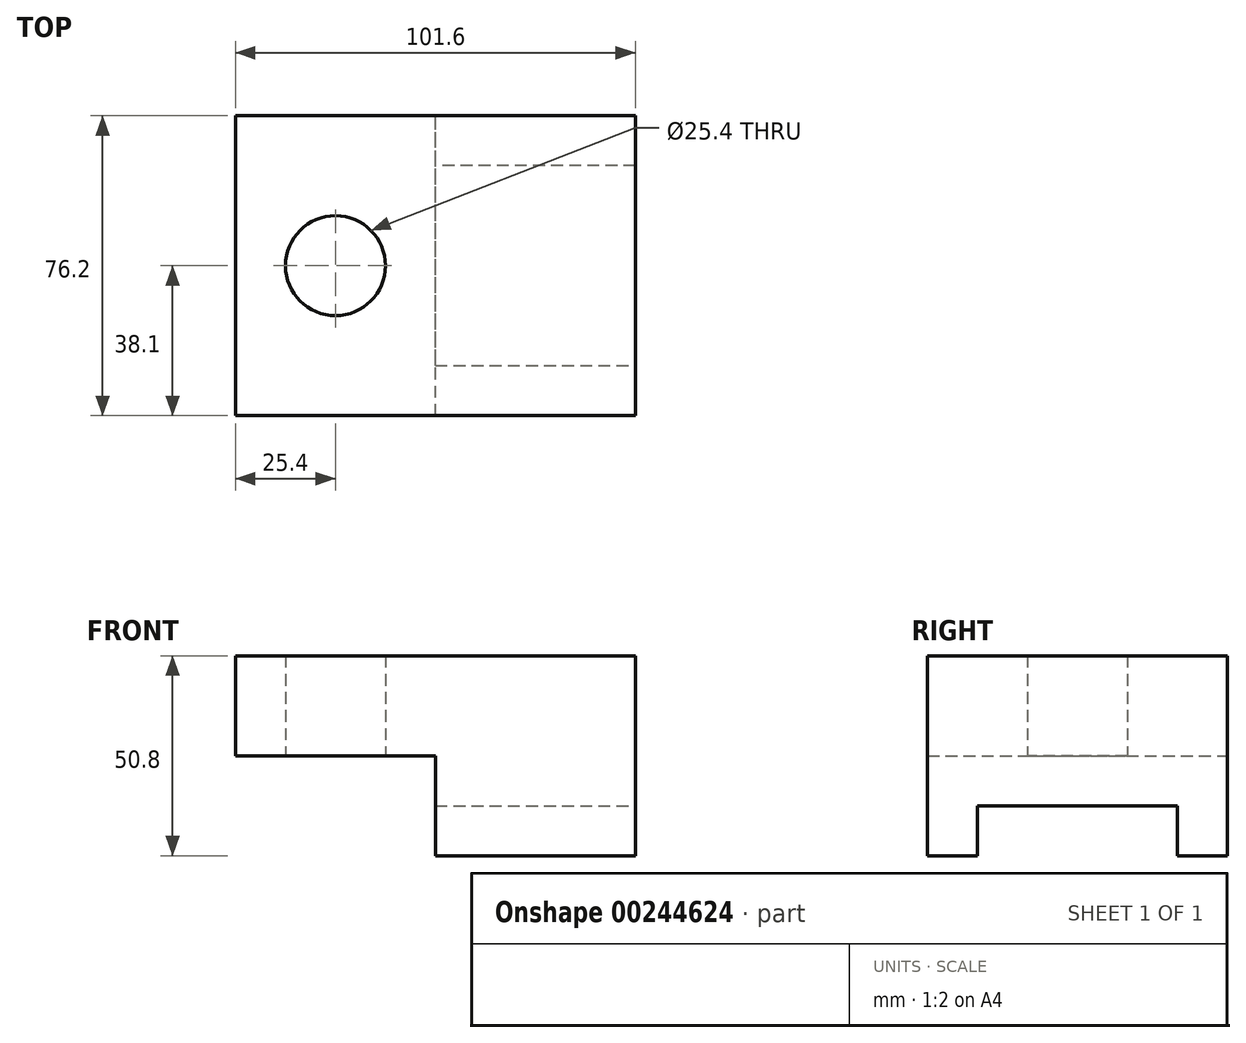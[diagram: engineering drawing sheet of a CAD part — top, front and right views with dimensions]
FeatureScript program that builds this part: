
annotation { "Feature Type Name" : "Feature", "Feature Type Description" : "" }
export const myFeature = defineFeature(function(context is Context, id is Id, definition is map)
    precondition{}
    {
        {
            var Q0;
            Q0=qCreatedBy(makeId("Top.planeOp"),FACE);
            var sketch = newSketch(context, id + "F0", { "sketchPlane" : qUnion([Q0])});
            skLineSegment(sketch, "E0.bottom", {"start": v(0, 0) * mm, "end": v(25.4, 0) * mm});
            skLineSegment(sketch, "E0.top", {"start": v(0, 25.4) * mm, "end": v(25.4, 25.4) * mm});
            skLineSegment(sketch, "E0.left", {"start": v(0, 0) * mm, "end": v(0, 25.4) * mm});
            skLineSegment(sketch, "E0.right", {"start": v(25.4, 0) * mm, "end": v(25.4, 25.4) * mm});
            skLineSegment(sketch, "E1.0.2.0", {"start": v(0, 50.8) * mm, "end": v(25.4, 50.8) * mm});
            skLineSegment(sketch, "E1.0.3.0", {"start": v(0, 76.2) * mm, "end": v(25.4, 76.2) * mm});
            skLineSegment(sketch, "E1.1.0.0", {"start": v(25.4, 0) * mm, "end": v(50.8, 0) * mm});
            skLineSegment(sketch, "E1.1.1.0", {"start": v(25.4, 25.4) * mm, "end": v(50.8, 25.4) * mm});
            skLineSegment(sketch, "E1.1.2.0", {"start": v(25.4, 50.8) * mm, "end": v(50.8, 50.8) * mm});
            skLineSegment(sketch, "E1.1.3.0", {"start": v(25.4, 76.2) * mm, "end": v(50.8, 76.2) * mm});
            skLineSegment(sketch, "E1.2.0.0", {"start": v(50.8, 0) * mm, "end": v(76.2, 0) * mm});
            skLineSegment(sketch, "E1.2.1.0", {"start": v(50.8, 25.4) * mm, "end": v(76.2, 25.4) * mm});
            skLineSegment(sketch, "E1.2.2.0", {"start": v(50.8, 50.8) * mm, "end": v(76.2, 50.8) * mm});
            skLineSegment(sketch, "E1.2.3.0", {"start": v(50.8, 76.2) * mm, "end": v(76.2, 76.2) * mm});
            skLineSegment(sketch, "E1.direction2", {"start": v(0, 0) * mm, "end": v(0, 25.4) * mm, "construction": true});
            skLineSegment(sketch, "E2", {"start": v(0, 76.2) * mm, "end": v(0, 50.8) * mm});
            skLineSegment(sketch, "E3", {"start": v(0, 50.8) * mm, "end": v(0, 25.4) * mm});
            skLineSegment(sketch, "E4", {"start": v(25.4, 76.2) * mm, "end": v(25.4, 50.8) * mm});
            skLineSegment(sketch, "E5", {"start": v(25.4, 50.8) * mm, "end": v(25.4, 25.4) * mm});
            skLineSegment(sketch, "E6", {"start": v(50.8, 76.2) * mm, "end": v(50.8, 50.8) * mm});
            skLineSegment(sketch, "E7", {"start": v(50.8, 50.8) * mm, "end": v(50.8, 25.4) * mm});
            skLineSegment(sketch, "E8", {"start": v(50.8, 25.4) * mm, "end": v(50.8, 0) * mm});
            skLineSegment(sketch, "E9", {"start": v(76.2, 76.2) * mm, "end": v(76.2, 50.8) * mm});
            skLineSegment(sketch, "E10", {"start": v(76.2, 25.4) * mm, "end": v(76.2, 0) * mm});
            skLineSegment(sketch, "E11.MirrorCS", {"start": v(0, 76.2) * mm, "end": v(-25.4, 76.2) * mm});
            skLineSegment(sketch, "E12.MirrorCS", {"start": v(-25.4, 50.8) * mm, "end": v(-25.4, 25.4) * mm});
            skLineSegment(sketch, "E13.MirrorCS", {"start": v(0, 25.4) * mm, "end": v(-25.4, 25.4) * mm});
            skLineSegment(sketch, "E14.MirrorCS", {"start": v(-25.4, 0) * mm, "end": v(-25.4, 25.4) * mm});
            skLineSegment(sketch, "E15.MirrorCS", {"start": v(0, 0) * mm, "end": v(-25.4, 0) * mm});
            skLineSegment(sketch, "E16.MirrorCS", {"start": v(0, 50.8) * mm, "end": v(-25.4, 50.8) * mm});
            skLineSegment(sketch, "E17.MirrorCS", {"start": v(-25.4, 76.2) * mm, "end": v(-25.4, 50.8) * mm});
            skLineSegment(sketch, "E18.MirrorCS", {"start": v(0, 0) * mm, "end": v(-25.4, 0) * mm, "construction": true});
            skLineSegment(sketch, "E19.MirrorCS", {"start": v(-25.4, 76.2) * mm, "end": v(-25.4, 101.6) * mm});
            skLineSegment(sketch, "E20.MirrorCS", {"start": v(0, 76.2) * mm, "end": v(0, 101.6) * mm});
            skLineSegment(sketch, "E21.MirrorCS", {"start": v(25.4, 76.2) * mm, "end": v(25.4, 101.6) * mm});
            skLineSegment(sketch, "E22.MirrorCS", {"start": v(50.8, 76.2) * mm, "end": v(50.8, 101.6) * mm});
            skLineSegment(sketch, "E23.MirrorCS", {"start": v(76.2, 76.2) * mm, "end": v(76.2, 101.6) * mm});
            skLineSegment(sketch, "E24.MirrorCS", {"start": v(50.8, 101.6) * mm, "end": v(76.2, 101.6) * mm});
            skLineSegment(sketch, "E25.MirrorCS", {"start": v(25.4, 101.6) * mm, "end": v(50.8, 101.6) * mm});
            skLineSegment(sketch, "E26.MirrorCS", {"start": v(0, 101.6) * mm, "end": v(25.4, 101.6) * mm});
            skLineSegment(sketch, "E27.MirrorCS", {"start": v(0, 101.6) * mm, "end": v(-25.4, 101.6) * mm});
            skCircle(sketch, "E28", {"center": v(-25.4, 101.6) * mm, "radius": 63.5 * mm});
            skSolve(sketch);
        }
        {
            var Q0;
            Q0=qCreatedBy(makeId("Front.planeOp"),FACE);
            var sketch = newSketch(context, id + "F1", { "sketchPlane" : qUnion([Q0])});
            skCircle(sketch, "E29.cCircle", {"center": v(0, 0) * mm, "radius": 6.35 * mm, "construction": true});
            skLineSegment(sketch, "E29.0", {"start": v(6.35, 4.61) * mm, "end": v(6.35, -4.61) * mm});
            skLineSegment(sketch, "E29.1", {"start": v(6.35, -4.61) * mm, "end": v(-2.43, -7.46) * mm});
            skLineSegment(sketch, "E29.2", {"start": v(-2.43, -7.46) * mm, "end": v(-7.85, 0) * mm});
            skLineSegment(sketch, "E29.3", {"start": v(-7.85, 0) * mm, "end": v(-2.43, 7.46) * mm});
            skLineSegment(sketch, "E29.4", {"start": v(-2.43, 7.46) * mm, "end": v(6.35, 4.61) * mm});
            skPoint(sketch, "E29.0.midPoint", {"position": v(6.35, 0) * mm});
            skSolve(sketch);
        }
        {
            var Q0;
            Q0=qCreatedBy(makeId("Right.planeOp"),FACE);
            var sketch = newSketch(context, id + "F2", { "sketchPlane" : qUnion([Q0])});
            skFitSpline(sketch, "E30", {"points": [v(0, 0) * mm, v(7.26, 7.32) * mm, v(17.34, -3.2) * mm, v(25.9, 0) * mm, v(31.53, -5.73) * mm, v(44.34, 3.11) * mm, v(50.55, -5.63) * mm, v(57.76, 0.91) * mm], "startDerivative": vector(54.1, 88.88) * mm, "endDerivative": vector(60.13, 87.54) * mm});
            skSolve(sketch);
        }
        {
            var Q0;
            Q0=qCreatedBy(makeId("Front.planeOp"),FACE);
            cPlane(context, id + "F3", {"entities" : qUnion([Q0]), "cplaneType" : CPlaneType.OFFSET, "offset" : 127 * mm, "width" : 152.4 * mm, "height" : 152.4 * mm});
        }
        {
            var Q0;
            Q0=qCreatedBy(id+"F3.planeOp",FACE);
            var sketch = newSketch(context, id + "F4", { "sketchPlane" : qUnion([Q0])});
            skCircle(sketch, "E31.cCircle", {"center": v(0, 0) * mm, "radius": 63.5 * mm, "construction": true});
            skLineSegment(sketch, "E31.0", {"start": v(55.53, 38.51) * mm, "end": v(67.3, -6.2) * mm});
            skLineSegment(sketch, "E31.1", {"start": v(67.3, -6.2) * mm, "end": v(47.57, -48) * mm});
            skLineSegment(sketch, "E31.2", {"start": v(47.57, -48) * mm, "end": v(5.59, -67.34) * mm});
            skLineSegment(sketch, "E31.3", {"start": v(5.59, -67.34) * mm, "end": v(-39, -55.18) * mm});
            skLineSegment(sketch, "E31.4", {"start": v(-39, -55.18) * mm, "end": v(-65.35, -17.2) * mm});
            skLineSegment(sketch, "E31.5", {"start": v(-65.35, -17.2) * mm, "end": v(-61.12, 28.83) * mm});
            skLineSegment(sketch, "E31.6", {"start": v(-61.12, 28.83) * mm, "end": v(-28.28, 61.37) * mm});
            skLineSegment(sketch, "E31.7", {"start": v(-28.28, 61.37) * mm, "end": v(17.78, 65.2) * mm});
            skLineSegment(sketch, "E31.8", {"start": v(17.78, 65.2) * mm, "end": v(55.53, 38.51) * mm});
            skPoint(sketch, "E31.0.midPoint", {"position": v(61.4, 16.16) * mm});
            skSolve(sketch);
        }
        {
            var Q0;
            Q0=qCreatedBy(makeId("Top.planeOp"),FACE);
            var sketch = newSketch(context, id + "F5", { "sketchPlane" : qUnion([Q0])});
            skLineSegment(sketch, "E32.bottom", {"start": v(0, 0) * mm, "end": v(101.6, 0) * mm});
            skLineSegment(sketch, "E32.top", {"start": v(0, 76.2) * mm, "end": v(101.6, 76.2) * mm});
            skLineSegment(sketch, "E32.left", {"start": v(0, 0) * mm, "end": v(0, 76.2) * mm});
            skLineSegment(sketch, "E32.right", {"start": v(101.6, 0) * mm, "end": v(101.6, 76.2) * mm});
            skSolve(sketch);
        }
        {
            var Q0;
            Q0=makeQuery(id+"F5.imprint","IMPRINT",FACE,{"disambiguationData":[TD([[makeQuery(id+"F5.imprint","IMPRINT",EDGE,{"derivedFrom":sQuery(id+"F5.wireOp",EDGE,"E32.bottom")}),1.0]])]});
            extrude(context, id + "F6", {"entities" : qUnion([Q0]), "depth" : 50.8 * mm});
        }
        {
            var Q0;
            Q0=qCreatedBy(makeId("Top.planeOp"),FACE);
            var sketch = newSketch(context, id + "F7", { "sketchPlane" : qUnion([Q0])});
            skLineSegment(sketch, "E33.bottom", {"start": v(0, 0) * mm, "end": v(50.8, 0) * mm});
            skLineSegment(sketch, "E33.top", {"start": v(0, 76.2) * mm, "end": v(50.8, 76.2) * mm});
            skLineSegment(sketch, "E33.left", {"start": v(0, 0) * mm, "end": v(0, 76.2) * mm});
            skLineSegment(sketch, "E33.right", {"start": v(50.8, 0) * mm, "end": v(50.8, 76.2) * mm});
            skSolve(sketch);
        }
        {
            var Q0;
            Q0 = qSketchRegion(id + "F7", true);
            extrude(context, id + "F8", {"entities" : qUnion([Q0]), "operationType" : NewBodyOperationType.REMOVE, "depth" : 25.4 * mm});
        }
        {
            var Q0;
            Q0=qCreatedBy(makeId("Top.planeOp"),FACE);
            var sketch = newSketch(context, id + "F9", { "sketchPlane" : qUnion([Q0])});
            skLineSegment(sketch, "E34", {"start": v(25.4, 0) * mm, "end": v(25.4, 38.1) * mm, "construction": true});
            skLineSegment(sketch, "E35", {"start": v(25.4, 38.1) * mm, "end": v(0, 38.1) * mm, "construction": true});
            skCircle(sketch, "E36", {"center": v(25.4, 38.1) * mm, "radius": 12.7 * mm});
            skSolve(sketch);
        }
        {
            var Q0;
            Q0=makeQuery(id+"F9.imprint","IMPRINT",FACE,{"disambiguationData":[TD([[makeQuery(id+"F9.imprint","IMPRINT",EDGE,{"derivedFrom":sQuery(id+"F9.wireOp",EDGE,"E36")}),1.0]])]});
            var Q1;
            Q1=sQuery(id+"F9.wireOp",EDGE,"E36");
            extrude(context, id + "F10", {"entities" : qUnion([Q0]), "operationType" : NewBodyOperationType.REMOVE, "surfaceEntities" : qUnion([Q1]), "depth" : 76.2 * mm});
        }
        {
            var Q0;
            Q0=makeQuery(id+"F6.opExtrude","CAP_FACE",FACE,{"disambiguationData":[OSD([sQuery(id+"F5.wireOp",EDGE,"E32.bottom"),sQuery(id+"F5.wireOp",EDGE,"E32.top"),sQuery(id+"F5.wireOp",EDGE,"E32.left"),sQuery(id+"F5.wireOp",EDGE,"E32.right")])],"isStart":true});
            var sketch = newSketch(context, id + "F11", { "sketchPlane" : qUnion([Q0])});
            skLineSegment(sketch, "E37", {"start": v(83.25, 0) * mm, "end": v(83.25, -12.7) * mm, "construction": true});
            skLineSegment(sketch, "E38", {"start": v(83.25, -12.7) * mm, "end": v(83.25, -63.5) * mm, "construction": true});
            skLineSegment(sketch, "E39", {"start": v(83.25, -63.5) * mm, "end": v(83.25, -76.2) * mm, "construction": true});
            skLineSegment(sketch, "E40", {"start": v(83.25, -12.7) * mm, "end": v(50.8, -12.7) * mm});
            skLineSegment(sketch, "E41", {"start": v(50.8, -12.7) * mm, "end": v(101.6, -12.7) * mm});
            skLineSegment(sketch, "E42", {"start": v(101.6, -12.7) * mm, "end": v(101.6, -63.5) * mm});
            skLineSegment(sketch, "E43", {"start": v(101.6, -63.5) * mm, "end": v(50.8, -63.5) * mm});
            skLineSegment(sketch, "E44", {"start": v(50.8, -63.5) * mm, "end": v(50.8, -12.7) * mm});
            skSolve(sketch);
        }
        {
            var Q0;
            {var subQ0=sQuery(id+"F11.wireOp",EDGE,"E42");Q0=makeQuery(id+"F11.imprint","IMPRINT",FACE,{"disambiguationData":[TD([[makeQuery(id+"F11.imprint","IMPRINT",EDGE,{"derivedFrom":subQ0}),-1.0]])]});}
            extrude(context, id + "F12", {"entities" : qUnion([Q0]), "operationType" : NewBodyOperationType.REMOVE, "oppositeDirection" : true, "depth" : 12.7 * mm});
        }
    });
